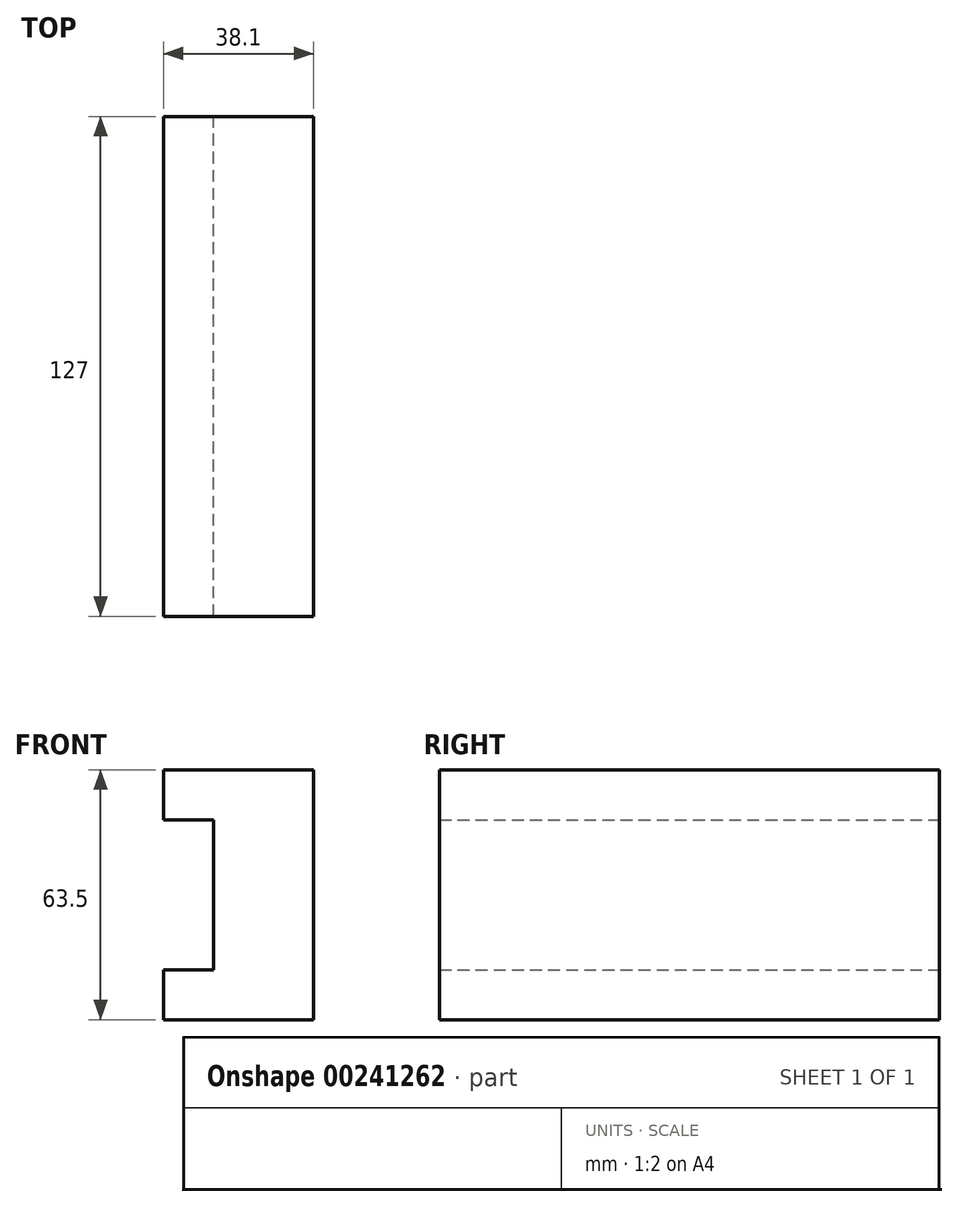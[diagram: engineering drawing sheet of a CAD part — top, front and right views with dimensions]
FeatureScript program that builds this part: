
annotation { "Feature Type Name" : "Feature", "Feature Type Description" : "" }
export const myFeature = defineFeature(function(context is Context, id is Id, definition is map)
    precondition{}
    {
        {
            var Q0;
            Q0=qCreatedBy(makeId("Front.planeOp"),FACE);
            var sketch = newSketch(context, id + "F0", { "sketchPlane" : qUnion([Q0])});
            skLineSegment(sketch, "E0", {"start": v(0, 0) * mm, "end": v(38.1, 0) * mm});
            skLineSegment(sketch, "E1", {"start": v(38.1, 0) * mm, "end": v(38.1, 63.5) * mm});
            skLineSegment(sketch, "E2", {"start": v(38.1, 63.5) * mm, "end": v(0, 63.5) * mm});
            skLineSegment(sketch, "E3", {"start": v(0, 63.5) * mm, "end": v(0, 50.8) * mm});
            skLineSegment(sketch, "E4", {"start": v(0, 50.8) * mm, "end": v(12.7, 50.8) * mm});
            skLineSegment(sketch, "E5", {"start": v(0, 0) * mm, "end": v(0, 12.7) * mm});
            skLineSegment(sketch, "E6", {"start": v(0, 12.7) * mm, "end": v(12.7, 12.7) * mm});
            skPoint(sketch, "E7.end.orphan", {"position": v(15.17, 12.7) * mm});
            skLineSegment(sketch, "E8", {"start": v(12.7, 50.8) * mm, "end": v(12.7, 12.7) * mm});
            skSolve(sketch);
        }
        {
            var Q0;
            Q0=makeQuery(id+"F0.imprint","IMPRINT",FACE,{"disambiguationData":[TD([[makeQuery(id+"F0.imprint","IMPRINT",EDGE,{"derivedFrom":sQuery(id+"F0.wireOp",EDGE,"E0")}),1.0]])]});
            extrude(context, id + "F1", {"entities" : qUnion([Q0]), "depth" : 127 * mm});
        }
    });
